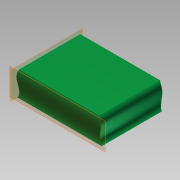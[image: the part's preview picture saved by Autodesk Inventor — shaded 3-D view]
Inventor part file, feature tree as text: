
AUTODESK INVENTOR PART (.ipt)
format: ipt  version: 2011 (Build 150239000, 239)  size: 121,344 bytes
history: native  units: mm
features: reference x4, other x3, extrude x3, sketch x3, projected_geometry x2
ambient origin geometry x8: Origin, YZ Plane, XZ Plane, XY Plane, X Axis, Y Axis, Z Axis, Center Point
feature tree (15):
  other  "Твердое тело1"
  extrude  "Выдавливание1"  Depth=0.3mm
  other  "РабПлоскость1"
  other  "РабПлоскость2"
  extrude  "Выдавливание2"  Depth=0.3mm
  extrude  "Выдавливание3"  Depth=0.3mm
  sketch  "Эскиз1"
  reference  "Ссылка1"
  reference  "Ссылка2"
  reference  "Ссылка3"
  reference  "Ссылка4"
  sketch  "Эскиз2"
  projected_geometry  "Спроецированная петля1"
  sketch  "Эскиз3"
  projected_geometry  "Спроецированная петля2"
